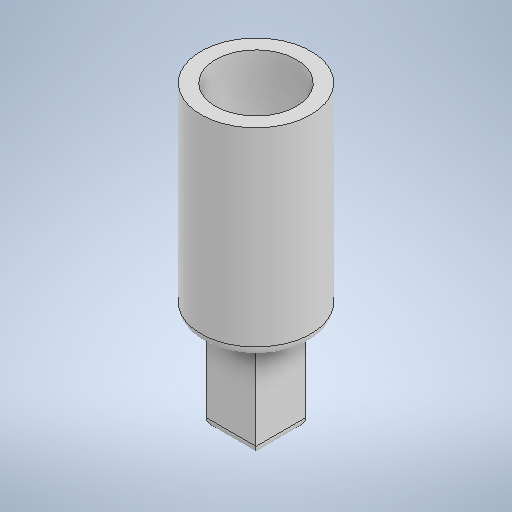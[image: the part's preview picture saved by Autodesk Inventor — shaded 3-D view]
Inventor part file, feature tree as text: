
AUTODESK INVENTOR PART (.ipt)
format: ipt  version: 2025.1 (Build 291241020, 241B)  size: 274,432 bytes
history: native  units: mm
features: sketch x4, extrude x4, fillet x2
ambient origin geometry x8: Origin, YZ Plane, XZ Plane, XY Plane, X Axis, Y Axis, Z Axis, Center Point
bodies: Solid1 (feature_tree)
feature tree (10):
  sketch  "Sketch1"  dims[d0=11.0mm d1=10.0mm d2=0.0mm]
  extrude  "Extrusion1"  Depth=10.0mm TaperAngle=0.0deg
  extrude  "Extrusion2"  Depth=5.0mm
  fillet  "Fillet1"  Radius=10.0mm
  fillet  "Fillet2"  Radius=1.0mm
  extrude  "Extrusion3"  Depth=1.0mm
  sketch  "Sketch3"  dims[d8=1.0mm d9=8.1mm]
  extrude  "Extrusion4"  Depth=5.0mm TaperAngle=0.0deg
  sketch  "Sketch2"  dims[d3=5.0mm d4=5.0mm d5=10.0mm d6=0.0mm d7=1.0mm]
  sketch  "Sketch4"  dims[d10=11.0mm d11=5.0mm d12=0.0mm d13=11.0mm d14=10.0mm d15=0.0mm d16=0.5mm d17=0.872665mm]
